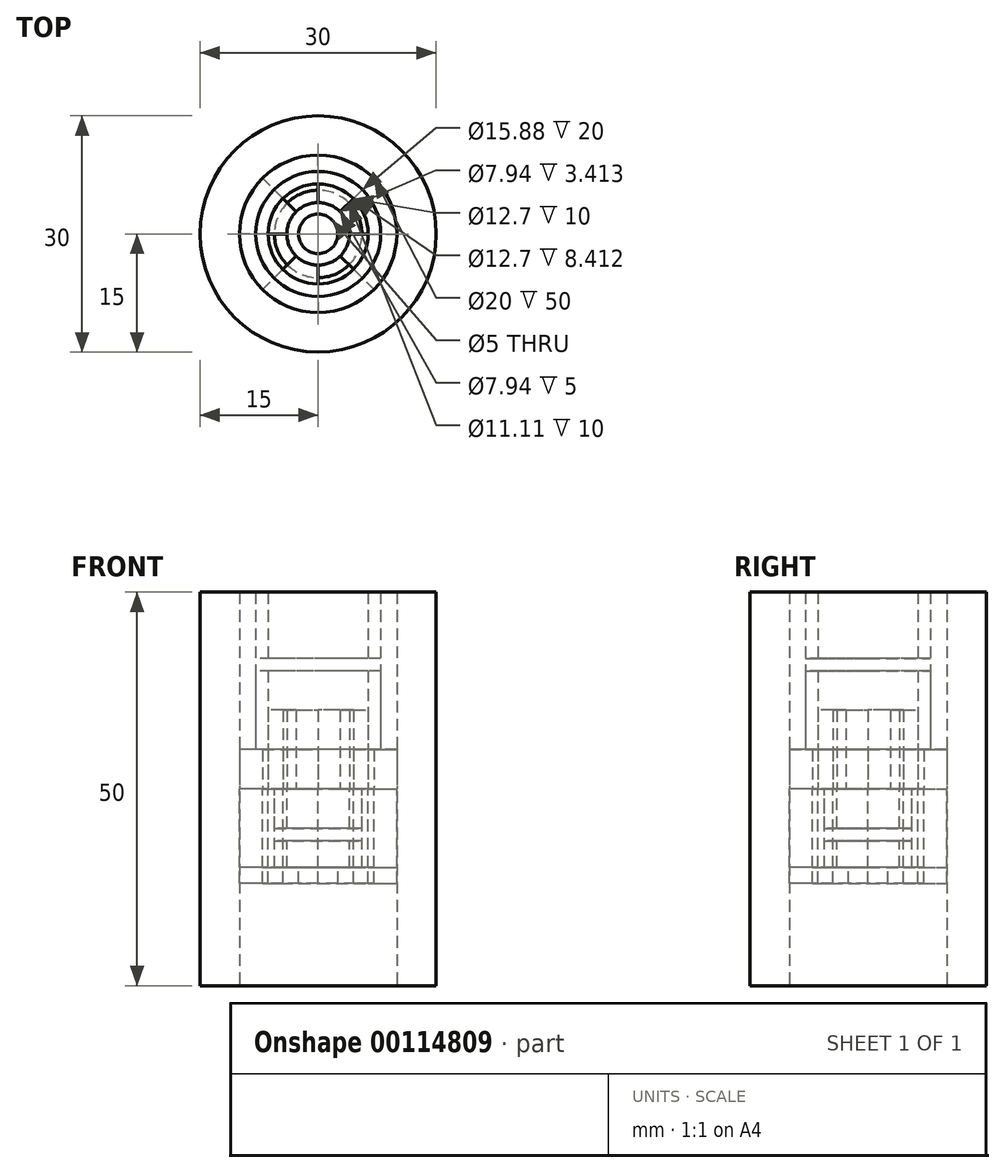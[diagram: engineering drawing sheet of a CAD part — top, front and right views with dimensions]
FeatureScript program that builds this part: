
annotation { "Feature Type Name" : "Feature", "Feature Type Description" : "" }
export const myFeature = defineFeature(function(context is Context, id is Id, definition is map)
    precondition{}
    {
        {
            var Q0;
            Q0=qCreatedBy(makeId("Top.planeOp"),FACE);
            var sketch = newSketch(context, id + "F0", { "sketchPlane" : qUnion([Q0])});
            skCircle(sketch, "E0", {"center": v(0, 0) * mm, "radius": 10 * mm});
            skCircle(sketch, "E1", {"center": v(0, 0) * mm, "radius": 3.97 * mm});
            skCircle(sketch, "E2", {"center": v(0, 0) * mm, "radius": 6.35 * mm});
            skCircle(sketch, "E3", {"center": v(0, 0) * mm, "radius": 7.94 * mm});
            skCircle(sketch, "E4", {"center": v(0, 0) * mm, "radius": 2.5 * mm});
            skLineSegment(sketch, "E5", {"start": v(0, 3.97) * mm, "end": v(0, 6.35) * mm});
            skLineSegment(sketch, "E6.1.0", {"start": v(-2.8, 2.8) * mm, "end": v(-4.5, 4.5) * mm});
            skLineSegment(sketch, "E6.2.0", {"start": v(-3.97, 0) * mm, "end": v(-6.35, 0) * mm});
            skLineSegment(sketch, "E6.3.0", {"start": v(-2.8, -2.8) * mm, "end": v(-4.5, -4.5) * mm});
            skLineSegment(sketch, "E6.4.0", {"start": v(0, -3.97) * mm, "end": v(0, -6.35) * mm});
            skLineSegment(sketch, "E6.5.0", {"start": v(2.8, -2.8) * mm, "end": v(4.5, -4.5) * mm});
            skLineSegment(sketch, "E6.6.0", {"start": v(3.97, 0) * mm, "end": v(6.35, 0) * mm});
            skLineSegment(sketch, "E6.7.0", {"start": v(2.8, 2.8) * mm, "end": v(4.5, 4.5) * mm});
            skCircle(sketch, "E7", {"center": v(0, 0) * mm, "radius": 15 * mm});
            skCircle(sketch, "E8", {"center": v(0, 0) * mm, "radius": 5.56 * mm});
            skLineSegment(sketch, "E9", {"start": v(0, 6.35) * mm, "end": v(0, 10) * mm});
            skLineSegment(sketch, "E10.1.0", {"start": v(-4.5, 4.5) * mm, "end": v(-7.07, 7.07) * mm});
            skLineSegment(sketch, "E10.2.0", {"start": v(-6.35, 0) * mm, "end": v(-10, 0) * mm});
            skLineSegment(sketch, "E11.1.3.0", {"start": v(-4.5, -4.5) * mm, "end": v(-7.07, -7.07) * mm});
            skLineSegment(sketch, "E11.1.4.0", {"start": v(0, -6.35) * mm, "end": v(0, -10) * mm});
            skLineSegment(sketch, "E11.1.5.0", {"start": v(4.5, -4.5) * mm, "end": v(7.07, -7.07) * mm});
            skLineSegment(sketch, "E11.1.6.0", {"start": v(6.35, 0) * mm, "end": v(10, 0) * mm});
            skLineSegment(sketch, "E11.1.7.0", {"start": v(4.5, 4.5) * mm, "end": v(7.07, 7.07) * mm});
            skSolve(sketch);
        }
        {
            var Q0;
            {var subQ0=sQuery(id+"F0.wireOp",EDGE,"E5");Q0=makeQuery(id+"F0.imprint","IMPRINT",FACE,{"disambiguationData":[TD([[makeQuery(id+"F0.imprint","IMPRINT",EDGE,{"derivedFrom":subQ0}),-1.0]])]});}
            var Q1;
            {var subQ0=sQuery(id+"F0.wireOp",EDGE,"E6.9.0");Q1=makeQuery(id+"F0.imprint","IMPRINT",FACE,{"disambiguationData":[TD([[makeQuery(id+"F0.imprint","IMPRINT",EDGE,{"derivedFrom":subQ0}),1.0]])]});}
            var Q2;
            {var subQ0=sQuery(id+"F0.wireOp",EDGE,"E6.7.0");Q2=makeQuery(id+"F0.imprint","IMPRINT",FACE,{"disambiguationData":[TD([[makeQuery(id+"F0.imprint","IMPRINT",EDGE,{"derivedFrom":subQ0}),1.0]])]});}
            var Q3;
            {var subQ0=sQuery(id+"F0.wireOp",EDGE,"E6.5.0");Q3=makeQuery(id+"F0.imprint","IMPRINT",FACE,{"disambiguationData":[TD([[makeQuery(id+"F0.imprint","IMPRINT",EDGE,{"derivedFrom":subQ0}),1.0]])]});}
            var Q4;
            {var subQ0=sQuery(id+"F0.wireOp",EDGE,"E6.3.0");Q4=makeQuery(id+"F0.imprint","IMPRINT",FACE,{"disambiguationData":[TD([[makeQuery(id+"F0.imprint","IMPRINT",EDGE,{"derivedFrom":subQ0}),1.0]])]});}
            var Q5;
            {var subQ0=sQuery(id+"F0.wireOp",EDGE,"E6.1.0");Q5=makeQuery(id+"F0.imprint","IMPRINT",FACE,{"disambiguationData":[TD([[makeQuery(id+"F0.imprint","IMPRINT",EDGE,{"derivedFrom":subQ0}),1.0]])]});}
            extrude(context, id + "F1", {"entities" : qUnion([Q0, Q1, Q2, Q3, Q4, Q5]), "depth" : 10 * mm});
        }
        {
            var Q0;
            Q0=makeQuery(id+"F0.imprint","IMPRINT",FACE,{"disambiguationData":[TD([[makeQuery(id+"F0.imprint","IMPRINT",EDGE,{"derivedFrom":sQuery(id+"F0.wireOp",EDGE,"E3")}),1.0]])]});
            extrude(context, id + "F2", {"entities" : qUnion([Q0]), "depth" : 15 * mm, "hasSecondDirection" : true, "secondDirectionOppositeDirection" : false, "secondDirectionDepth" : 5 * mm});
        }
        {
            var Q0;
            Q0=makeQuery(id+"F2.opExtrude","CAP_FACE",FACE,{"disambiguationData":[OSD([sQuery(id+"F0.wireOp",EDGE,"E2"),sQuery(id+"F0.wireOp",EDGE,"E3")])],"isStart":false});
            extrude(context, id + "F3", {"entities" : qUnion([Q0]), "operationType" : NewBodyOperationType.ADD, "depth" : 10 * mm, "hasSecondDirection" : true, "secondDirectionOppositeDirection" : false, "secondDirectionDepth" : 1.59 * mm});
        }
        {
            var Q0;
            Q0=makeQuery(id+"F0.imprint","IMPRINT",FACE,{"disambiguationData":[TD([[makeQuery(id+"F0.imprint","IMPRINT",EDGE,{"derivedFrom":sQuery(id+"F0.wireOp",EDGE,"E0")}),1.0]])]});
            extrude(context, id + "F4", {"entities" : qUnion([Q0]), "depth" : 25 * mm, "hasSecondDirection" : true, "secondDirectionOppositeDirection" : false, "secondDirectionDepth" : 5 * mm});
        }
        {
            var Q0;
            {var subQ0=sQuery(id+"F0.wireOp",EDGE,"E6.8.0");var subQ1=sQuery(id+"F0.wireOp",EDGE,"E1");var subQ2=makeQuery(id+"F0.imprint","INTERSECT",VERTEX,{"derivedFrom":[subQ1,subQ0]});Q0=makeQuery(id+"F0.imprint","IMPRINT",FACE,{"disambiguationData":[TD([[makeQuery(id+"F0.imprint","IMPRINT",EDGE,{"disambiguationData":[TD([[subQ2,-1.0]])],"derivedFrom":subQ1}),-1.0]])]});}
            var Q1;
            {var subQ0=sQuery(id+"F0.wireOp",EDGE,"E6.9.0");var subQ1=sQuery(id+"F0.wireOp",EDGE,"E1");var subQ2=makeQuery(id+"F0.imprint","INTERSECT",VERTEX,{"derivedFrom":[subQ1,subQ0]});Q1=makeQuery(id+"F0.imprint","IMPRINT",FACE,{"disambiguationData":[TD([[makeQuery(id+"F0.imprint","IMPRINT",EDGE,{"disambiguationData":[TD([[subQ2,-1.0]])],"derivedFrom":subQ1}),-1.0]])]});}
            var Q2;
            {var subQ0=sQuery(id+"F0.wireOp",EDGE,"E6.10.0");var subQ1=sQuery(id+"F0.wireOp",EDGE,"E1");var subQ2=makeQuery(id+"F0.imprint","INTERSECT",VERTEX,{"derivedFrom":[subQ1,subQ0]});Q2=makeQuery(id+"F0.imprint","IMPRINT",FACE,{"disambiguationData":[TD([[makeQuery(id+"F0.imprint","IMPRINT",EDGE,{"disambiguationData":[TD([[subQ2,-1.0]])],"derivedFrom":subQ1}),-1.0]])]});}
            var Q3;
            {var subQ0=sQuery(id+"F0.wireOp",EDGE,"E5");var subQ1=sQuery(id+"F0.wireOp",EDGE,"E1");var subQ2=makeQuery(id+"F0.imprint","INTERSECT",VERTEX,{"derivedFrom":[subQ1,subQ0]});Q3=makeQuery(id+"F0.imprint","IMPRINT",FACE,{"disambiguationData":[TD([[makeQuery(id+"F0.imprint","IMPRINT",EDGE,{"disambiguationData":[TD([[subQ2,1.0]])],"derivedFrom":subQ1}),-1.0]])]});}
            var Q4;
            {var subQ0=sQuery(id+"F0.wireOp",EDGE,"E5");var subQ1=sQuery(id+"F0.wireOp",EDGE,"E1");var subQ2=makeQuery(id+"F0.imprint","INTERSECT",VERTEX,{"derivedFrom":[subQ1,subQ0]});Q4=makeQuery(id+"F0.imprint","IMPRINT",FACE,{"disambiguationData":[TD([[makeQuery(id+"F0.imprint","IMPRINT",EDGE,{"disambiguationData":[TD([[subQ2,-1.0]])],"derivedFrom":subQ1}),-1.0]])]});}
            var Q5;
            {var subQ0=sQuery(id+"F0.wireOp",EDGE,"E6.1.0");var subQ1=sQuery(id+"F0.wireOp",EDGE,"E1");var subQ2=makeQuery(id+"F0.imprint","INTERSECT",VERTEX,{"derivedFrom":[subQ1,subQ0]});Q5=makeQuery(id+"F0.imprint","IMPRINT",FACE,{"disambiguationData":[TD([[makeQuery(id+"F0.imprint","IMPRINT",EDGE,{"disambiguationData":[TD([[subQ2,-1.0]])],"derivedFrom":subQ1}),-1.0]])]});}
            var Q6;
            {var subQ0=sQuery(id+"F0.wireOp",EDGE,"E6.2.0");var subQ1=sQuery(id+"F0.wireOp",EDGE,"E1");var subQ2=makeQuery(id+"F0.imprint","INTERSECT",VERTEX,{"derivedFrom":[subQ1,subQ0]});Q6=makeQuery(id+"F0.imprint","IMPRINT",FACE,{"disambiguationData":[TD([[makeQuery(id+"F0.imprint","IMPRINT",EDGE,{"disambiguationData":[TD([[subQ2,-1.0]])],"derivedFrom":subQ1}),-1.0]])]});}
            var Q7;
            {var subQ0=sQuery(id+"F0.wireOp",EDGE,"E6.3.0");var subQ1=sQuery(id+"F0.wireOp",EDGE,"E1");var subQ2=makeQuery(id+"F0.imprint","INTERSECT",VERTEX,{"derivedFrom":[subQ1,subQ0]});Q7=makeQuery(id+"F0.imprint","IMPRINT",FACE,{"disambiguationData":[TD([[makeQuery(id+"F0.imprint","IMPRINT",EDGE,{"disambiguationData":[TD([[subQ2,-1.0]])],"derivedFrom":subQ1}),-1.0]])]});}
            var Q8;
            {var subQ0=sQuery(id+"F0.wireOp",EDGE,"E6.4.0");var subQ1=sQuery(id+"F0.wireOp",EDGE,"E1");var subQ2=makeQuery(id+"F0.imprint","INTERSECT",VERTEX,{"derivedFrom":[subQ1,subQ0]});Q8=makeQuery(id+"F0.imprint","IMPRINT",FACE,{"disambiguationData":[TD([[makeQuery(id+"F0.imprint","IMPRINT",EDGE,{"disambiguationData":[TD([[subQ2,-1.0]])],"derivedFrom":subQ1}),-1.0]])]});}
            var Q9;
            {var subQ0=sQuery(id+"F0.wireOp",EDGE,"E6.5.0");var subQ1=sQuery(id+"F0.wireOp",EDGE,"E1");var subQ2=makeQuery(id+"F0.imprint","INTERSECT",VERTEX,{"derivedFrom":[subQ1,subQ0]});Q9=makeQuery(id+"F0.imprint","IMPRINT",FACE,{"disambiguationData":[TD([[makeQuery(id+"F0.imprint","IMPRINT",EDGE,{"disambiguationData":[TD([[subQ2,-1.0]])],"derivedFrom":subQ1}),-1.0]])]});}
            var Q10;
            {var subQ0=sQuery(id+"F0.wireOp",EDGE,"E6.6.0");var subQ1=sQuery(id+"F0.wireOp",EDGE,"E1");var subQ2=makeQuery(id+"F0.imprint","INTERSECT",VERTEX,{"derivedFrom":[subQ1,subQ0]});Q10=makeQuery(id+"F0.imprint","IMPRINT",FACE,{"disambiguationData":[TD([[makeQuery(id+"F0.imprint","IMPRINT",EDGE,{"disambiguationData":[TD([[subQ2,-1.0]])],"derivedFrom":subQ1}),-1.0]])]});}
            var Q11;
            {var subQ0=sQuery(id+"F0.wireOp",EDGE,"E6.7.0");var subQ1=sQuery(id+"F0.wireOp",EDGE,"E1");var subQ2=makeQuery(id+"F0.imprint","INTERSECT",VERTEX,{"derivedFrom":[subQ1,subQ0]});Q11=makeQuery(id+"F0.imprint","IMPRINT",FACE,{"disambiguationData":[TD([[makeQuery(id+"F0.imprint","IMPRINT",EDGE,{"disambiguationData":[TD([[subQ2,-1.0]])],"derivedFrom":subQ1}),-1.0]])]});}
            extrude(context, id + "F5", {"entities" : qUnion([Q0, Q1, Q2, Q3, Q4, Q5, Q6, Q7, Q8, Q9, Q10, Q11]), "oppositeDirection" : true, "depth" : 10 * mm, "hasSecondDirection" : true, "secondDirectionOppositeDirection" : true, "secondDirectionDepth" : 6.6 * mm});
        }
        {
            var Q0;
            {var subQ0=sQuery(id+"F0.wireOp",EDGE,"E6.8.0");var subQ1=sQuery(id+"F0.wireOp",EDGE,"E1");var subQ2=makeQuery(id+"F0.imprint","INTERSECT",VERTEX,{"derivedFrom":[subQ1,subQ0]});Q0=makeQuery(id+"F0.imprint","IMPRINT",FACE,{"disambiguationData":[TD([[makeQuery(id+"F0.imprint","IMPRINT",EDGE,{"disambiguationData":[TD([[subQ2,-1.0]])],"derivedFrom":subQ1}),-1.0]])]});}
            var Q1;
            {var subQ0=sQuery(id+"F0.wireOp",EDGE,"E6.9.0");var subQ1=sQuery(id+"F0.wireOp",EDGE,"E1");var subQ2=makeQuery(id+"F0.imprint","INTERSECT",VERTEX,{"derivedFrom":[subQ1,subQ0]});Q1=makeQuery(id+"F0.imprint","IMPRINT",FACE,{"disambiguationData":[TD([[makeQuery(id+"F0.imprint","IMPRINT",EDGE,{"disambiguationData":[TD([[subQ2,-1.0]])],"derivedFrom":subQ1}),-1.0]])]});}
            var Q2;
            {var subQ0=sQuery(id+"F0.wireOp",EDGE,"E6.10.0");var subQ1=sQuery(id+"F0.wireOp",EDGE,"E1");var subQ2=makeQuery(id+"F0.imprint","INTERSECT",VERTEX,{"derivedFrom":[subQ1,subQ0]});Q2=makeQuery(id+"F0.imprint","IMPRINT",FACE,{"disambiguationData":[TD([[makeQuery(id+"F0.imprint","IMPRINT",EDGE,{"disambiguationData":[TD([[subQ2,-1.0]])],"derivedFrom":subQ1}),-1.0]])]});}
            var Q3;
            {var subQ0=sQuery(id+"F0.wireOp",EDGE,"E5");var subQ1=sQuery(id+"F0.wireOp",EDGE,"E1");var subQ2=makeQuery(id+"F0.imprint","INTERSECT",VERTEX,{"derivedFrom":[subQ1,subQ0]});Q3=makeQuery(id+"F0.imprint","IMPRINT",FACE,{"disambiguationData":[TD([[makeQuery(id+"F0.imprint","IMPRINT",EDGE,{"disambiguationData":[TD([[subQ2,1.0]])],"derivedFrom":subQ1}),-1.0]])]});}
            var Q4;
            {var subQ0=sQuery(id+"F0.wireOp",EDGE,"E5");var subQ1=sQuery(id+"F0.wireOp",EDGE,"E1");var subQ2=makeQuery(id+"F0.imprint","INTERSECT",VERTEX,{"derivedFrom":[subQ1,subQ0]});Q4=makeQuery(id+"F0.imprint","IMPRINT",FACE,{"disambiguationData":[TD([[makeQuery(id+"F0.imprint","IMPRINT",EDGE,{"disambiguationData":[TD([[subQ2,-1.0]])],"derivedFrom":subQ1}),-1.0]])]});}
            var Q5;
            {var subQ0=sQuery(id+"F0.wireOp",EDGE,"E6.1.0");var subQ1=sQuery(id+"F0.wireOp",EDGE,"E1");var subQ2=makeQuery(id+"F0.imprint","INTERSECT",VERTEX,{"derivedFrom":[subQ1,subQ0]});Q5=makeQuery(id+"F0.imprint","IMPRINT",FACE,{"disambiguationData":[TD([[makeQuery(id+"F0.imprint","IMPRINT",EDGE,{"disambiguationData":[TD([[subQ2,-1.0]])],"derivedFrom":subQ1}),-1.0]])]});}
            var Q6;
            {var subQ0=sQuery(id+"F0.wireOp",EDGE,"E6.2.0");var subQ1=sQuery(id+"F0.wireOp",EDGE,"E1");var subQ2=makeQuery(id+"F0.imprint","INTERSECT",VERTEX,{"derivedFrom":[subQ1,subQ0]});Q6=makeQuery(id+"F0.imprint","IMPRINT",FACE,{"disambiguationData":[TD([[makeQuery(id+"F0.imprint","IMPRINT",EDGE,{"disambiguationData":[TD([[subQ2,-1.0]])],"derivedFrom":subQ1}),-1.0]])]});}
            var Q7;
            {var subQ0=sQuery(id+"F0.wireOp",EDGE,"E6.3.0");var subQ1=sQuery(id+"F0.wireOp",EDGE,"E1");var subQ2=makeQuery(id+"F0.imprint","INTERSECT",VERTEX,{"derivedFrom":[subQ1,subQ0]});Q7=makeQuery(id+"F0.imprint","IMPRINT",FACE,{"disambiguationData":[TD([[makeQuery(id+"F0.imprint","IMPRINT",EDGE,{"disambiguationData":[TD([[subQ2,-1.0]])],"derivedFrom":subQ1}),-1.0]])]});}
            var Q8;
            {var subQ0=sQuery(id+"F0.wireOp",EDGE,"E6.4.0");var subQ1=sQuery(id+"F0.wireOp",EDGE,"E1");var subQ2=makeQuery(id+"F0.imprint","INTERSECT",VERTEX,{"derivedFrom":[subQ1,subQ0]});Q8=makeQuery(id+"F0.imprint","IMPRINT",FACE,{"disambiguationData":[TD([[makeQuery(id+"F0.imprint","IMPRINT",EDGE,{"disambiguationData":[TD([[subQ2,-1.0]])],"derivedFrom":subQ1}),-1.0]])]});}
            var Q9;
            {var subQ0=sQuery(id+"F0.wireOp",EDGE,"E6.5.0");var subQ1=sQuery(id+"F0.wireOp",EDGE,"E1");var subQ2=makeQuery(id+"F0.imprint","INTERSECT",VERTEX,{"derivedFrom":[subQ1,subQ0]});Q9=makeQuery(id+"F0.imprint","IMPRINT",FACE,{"disambiguationData":[TD([[makeQuery(id+"F0.imprint","IMPRINT",EDGE,{"disambiguationData":[TD([[subQ2,-1.0]])],"derivedFrom":subQ1}),-1.0]])]});}
            var Q10;
            {var subQ0=sQuery(id+"F0.wireOp",EDGE,"E6.6.0");var subQ1=sQuery(id+"F0.wireOp",EDGE,"E1");var subQ2=makeQuery(id+"F0.imprint","INTERSECT",VERTEX,{"derivedFrom":[subQ1,subQ0]});Q10=makeQuery(id+"F0.imprint","IMPRINT",FACE,{"disambiguationData":[TD([[makeQuery(id+"F0.imprint","IMPRINT",EDGE,{"disambiguationData":[TD([[subQ2,-1.0]])],"derivedFrom":subQ1}),-1.0]])]});}
            var Q11;
            {var subQ0=sQuery(id+"F0.wireOp",EDGE,"E6.7.0");var subQ1=sQuery(id+"F0.wireOp",EDGE,"E1");var subQ2=makeQuery(id+"F0.imprint","INTERSECT",VERTEX,{"derivedFrom":[subQ1,subQ0]});Q11=makeQuery(id+"F0.imprint","IMPRINT",FACE,{"disambiguationData":[TD([[makeQuery(id+"F0.imprint","IMPRINT",EDGE,{"disambiguationData":[TD([[subQ2,-1.0]])],"derivedFrom":subQ1}),-1.0]])]});}
            extrude(context, id + "F6", {"entities" : qUnion([Q0, Q1, Q2, Q3, Q4, Q5, Q6, Q7, Q8, Q9, Q10, Q11]), "oppositeDirection" : true, "depth" : 5 * mm});
        }
        {
            var Q0;
            {var subQ0=sQuery(id+"F0.wireOp",EDGE,"E6.5.0");var subQ5=sQuery(id+"F0.wireOp",EDGE,"E8");var subQ6=makeQuery(id+"F0.imprint","INTERSECT",VERTEX,{"derivedFrom":[subQ0,subQ5]});Q0=makeQuery(id+"F0.imprint","IMPRINT",FACE,{"disambiguationData":[TD([[makeQuery(id+"F0.imprint","IMPRINT",EDGE,{"disambiguationData":[TD([[subQ6,-1.0]])],"derivedFrom":subQ5}),-1.0]])]});}
            var Q1;
            {var subQ0=sQuery(id+"F0.wireOp",EDGE,"E6.4.0");var subQ5=sQuery(id+"F0.wireOp",EDGE,"E8");var subQ6=makeQuery(id+"F0.imprint","INTERSECT",VERTEX,{"derivedFrom":[subQ0,subQ5]});Q1=makeQuery(id+"F0.imprint","IMPRINT",FACE,{"disambiguationData":[TD([[makeQuery(id+"F0.imprint","IMPRINT",EDGE,{"disambiguationData":[TD([[subQ6,-1.0]])],"derivedFrom":subQ5}),-1.0]])]});}
            var Q2;
            {var subQ0=sQuery(id+"F0.wireOp",EDGE,"E6.3.0");var subQ5=sQuery(id+"F0.wireOp",EDGE,"E8");var subQ6=makeQuery(id+"F0.imprint","INTERSECT",VERTEX,{"derivedFrom":[subQ0,subQ5]});Q2=makeQuery(id+"F0.imprint","IMPRINT",FACE,{"disambiguationData":[TD([[makeQuery(id+"F0.imprint","IMPRINT",EDGE,{"disambiguationData":[TD([[subQ6,-1.0]])],"derivedFrom":subQ5}),-1.0]])]});}
            var Q3;
            {var subQ0=sQuery(id+"F0.wireOp",EDGE,"E6.2.0");var subQ5=sQuery(id+"F0.wireOp",EDGE,"E8");var subQ6=makeQuery(id+"F0.imprint","INTERSECT",VERTEX,{"derivedFrom":[subQ0,subQ5]});Q3=makeQuery(id+"F0.imprint","IMPRINT",FACE,{"disambiguationData":[TD([[makeQuery(id+"F0.imprint","IMPRINT",EDGE,{"disambiguationData":[TD([[subQ6,-1.0]])],"derivedFrom":subQ5}),-1.0]])]});}
            var Q4;
            {var subQ0=sQuery(id+"F0.wireOp",EDGE,"E6.1.0");var subQ5=sQuery(id+"F0.wireOp",EDGE,"E8");var subQ6=makeQuery(id+"F0.imprint","INTERSECT",VERTEX,{"derivedFrom":[subQ0,subQ5]});Q4=makeQuery(id+"F0.imprint","IMPRINT",FACE,{"disambiguationData":[TD([[makeQuery(id+"F0.imprint","IMPRINT",EDGE,{"disambiguationData":[TD([[subQ6,-1.0]])],"derivedFrom":subQ5}),-1.0]])]});}
            var Q5;
            {var subQ0=sQuery(id+"F0.wireOp",EDGE,"E5");var subQ5=sQuery(id+"F0.wireOp",EDGE,"E8");var subQ6=makeQuery(id+"F0.imprint","INTERSECT",VERTEX,{"derivedFrom":[subQ0,subQ5]});Q5=makeQuery(id+"F0.imprint","IMPRINT",FACE,{"disambiguationData":[TD([[makeQuery(id+"F0.imprint","IMPRINT",EDGE,{"disambiguationData":[TD([[subQ6,-1.0]])],"derivedFrom":subQ5}),-1.0]])]});}
            var Q6;
            {var subQ0=sQuery(id+"F0.wireOp",EDGE,"E5");var subQ5=sQuery(id+"F0.wireOp",EDGE,"E8");var subQ7=makeQuery(id+"F0.imprint","INTERSECT",VERTEX,{"derivedFrom":[subQ0,subQ5]});Q6=makeQuery(id+"F0.imprint","IMPRINT",FACE,{"disambiguationData":[TD([[makeQuery(id+"F0.imprint","IMPRINT",EDGE,{"disambiguationData":[TD([[subQ7,1.0]])],"derivedFrom":subQ5}),-1.0]])]});}
            var Q7;
            {var subQ0=sQuery(id+"F0.wireOp",EDGE,"E6.6.0");var subQ5=sQuery(id+"F0.wireOp",EDGE,"E8");var subQ7=makeQuery(id+"F0.imprint","INTERSECT",VERTEX,{"derivedFrom":[subQ0,subQ5]});Q7=makeQuery(id+"F0.imprint","IMPRINT",FACE,{"disambiguationData":[TD([[makeQuery(id+"F0.imprint","IMPRINT",EDGE,{"disambiguationData":[TD([[subQ7,-1.0]])],"derivedFrom":subQ5}),-1.0]])]});}
            var Q8;
            {var subQ0=sQuery(id+"F0.wireOp",EDGE,"E9");var subQ1=sQuery(id+"F0.wireOp",EDGE,"E0");var subQ2=makeQuery(id+"F0.imprint","INTERSECT",VERTEX,{"derivedFrom":[subQ1,subQ0]});Q8=makeQuery(id+"F0.imprint","IMPRINT",FACE,{"disambiguationData":[TD([[makeQuery(id+"F0.imprint","IMPRINT",EDGE,{"disambiguationData":[TD([[subQ2,1.0]])],"derivedFrom":subQ1}),1.0]])]});}
            var Q9;
            {var subQ3=sQuery(id+"F0.wireOp",EDGE,"E11.1.7.0");var subQ5=sQuery(id+"F0.wireOp",EDGE,"E3");var subQ6=makeQuery(id+"F0.imprint","INTERSECT",VERTEX,{"derivedFrom":[subQ5,subQ3]});Q9=makeQuery(id+"F0.imprint","IMPRINT",FACE,{"disambiguationData":[TD([[makeQuery(id+"F0.imprint","IMPRINT",EDGE,{"disambiguationData":[TD([[subQ6,-1.0]])],"derivedFrom":subQ5}),1.0]])]});}
            var Q10;
            {var subQ0=sQuery(id+"F0.wireOp",EDGE,"E10.1.0");var subQ5=sQuery(id+"F0.wireOp",EDGE,"E3");var subQ6=makeQuery(id+"F0.imprint","INTERSECT",VERTEX,{"derivedFrom":[subQ5,subQ0]});Q10=makeQuery(id+"F0.imprint","IMPRINT",FACE,{"disambiguationData":[TD([[makeQuery(id+"F0.imprint","IMPRINT",EDGE,{"disambiguationData":[TD([[subQ6,-1.0]])],"derivedFrom":subQ5}),1.0]])]});}
            var Q11;
            {var subQ0=sQuery(id+"F0.wireOp",EDGE,"E10.1.0");var subQ1=sQuery(id+"F0.wireOp",EDGE,"E0");var subQ2=makeQuery(id+"F0.imprint","INTERSECT",VERTEX,{"derivedFrom":[subQ1,subQ0]});Q11=makeQuery(id+"F0.imprint","IMPRINT",FACE,{"disambiguationData":[TD([[makeQuery(id+"F0.imprint","IMPRINT",EDGE,{"disambiguationData":[TD([[subQ2,-1.0]])],"derivedFrom":subQ1}),1.0]])]});}
            var Q12;
            {var subQ0=sQuery(id+"F0.wireOp",EDGE,"E11.1.3.0");var subQ1=sQuery(id+"F0.wireOp",EDGE,"E0");var subQ2=makeQuery(id+"F0.imprint","INTERSECT",VERTEX,{"derivedFrom":[subQ1,subQ0]});Q12=makeQuery(id+"F0.imprint","IMPRINT",FACE,{"disambiguationData":[TD([[makeQuery(id+"F0.imprint","IMPRINT",EDGE,{"disambiguationData":[TD([[subQ2,-1.0]])],"derivedFrom":subQ1}),1.0]])]});}
            var Q13;
            {var subQ0=sQuery(id+"F0.wireOp",EDGE,"E11.1.3.0");var subQ5=sQuery(id+"F0.wireOp",EDGE,"E3");var subQ6=makeQuery(id+"F0.imprint","INTERSECT",VERTEX,{"derivedFrom":[subQ5,subQ0]});Q13=makeQuery(id+"F0.imprint","IMPRINT",FACE,{"disambiguationData":[TD([[makeQuery(id+"F0.imprint","IMPRINT",EDGE,{"disambiguationData":[TD([[subQ6,-1.0]])],"derivedFrom":subQ5}),1.0]])]});}
            var Q14;
            {var subQ0=sQuery(id+"F0.wireOp",EDGE,"E11.1.5.0");var subQ1=sQuery(id+"F0.wireOp",EDGE,"E0");var subQ2=makeQuery(id+"F0.imprint","INTERSECT",VERTEX,{"derivedFrom":[subQ1,subQ0]});Q14=makeQuery(id+"F0.imprint","IMPRINT",FACE,{"disambiguationData":[TD([[makeQuery(id+"F0.imprint","IMPRINT",EDGE,{"disambiguationData":[TD([[subQ2,-1.0]])],"derivedFrom":subQ1}),1.0]])]});}
            var Q15;
            {var subQ3=sQuery(id+"F0.wireOp",EDGE,"E11.1.6.0");var subQ5=sQuery(id+"F0.wireOp",EDGE,"E3");var subQ7=makeQuery(id+"F0.imprint","INTERSECT",VERTEX,{"derivedFrom":[subQ5,subQ3]});Q15=makeQuery(id+"F0.imprint","IMPRINT",FACE,{"disambiguationData":[TD([[makeQuery(id+"F0.imprint","IMPRINT",EDGE,{"disambiguationData":[TD([[subQ7,1.0]])],"derivedFrom":subQ5}),1.0]])]});}
            extrude(context, id + "F7", {"entities" : qUnion([Q0, Q1, Q2, Q3, Q4, Q5, Q6, Q7, Q8, Q9, Q10, Q11, Q12, Q13, Q14, Q15]), "oppositeDirection" : true, "depth" : 10 * mm});
        }
        {
            var Q0;
            {var subQ0=sQuery(id+"F0.wireOp",EDGE,"E9");var subQ1=sQuery(id+"F0.wireOp",EDGE,"E0");var subQ2=makeQuery(id+"F0.imprint","INTERSECT",VERTEX,{"derivedFrom":[subQ1,subQ0]});Q0=makeQuery(id+"F0.imprint","IMPRINT",FACE,{"disambiguationData":[TD([[makeQuery(id+"F0.imprint","IMPRINT",EDGE,{"disambiguationData":[TD([[subQ2,1.0]])],"derivedFrom":subQ1}),1.0]])]});}
            var Q1;
            {var subQ3=sQuery(id+"F0.wireOp",EDGE,"E11.1.7.0");var subQ5=sQuery(id+"F0.wireOp",EDGE,"E3");var subQ6=makeQuery(id+"F0.imprint","INTERSECT",VERTEX,{"derivedFrom":[subQ5,subQ3]});Q1=makeQuery(id+"F0.imprint","IMPRINT",FACE,{"disambiguationData":[TD([[makeQuery(id+"F0.imprint","IMPRINT",EDGE,{"disambiguationData":[TD([[subQ6,-1.0]])],"derivedFrom":subQ5}),1.0]])]});}
            var Q2;
            {var subQ0=sQuery(id+"F0.wireOp",EDGE,"E11.1.5.0");var subQ1=sQuery(id+"F0.wireOp",EDGE,"E0");var subQ2=makeQuery(id+"F0.imprint","INTERSECT",VERTEX,{"derivedFrom":[subQ1,subQ0]});Q2=makeQuery(id+"F0.imprint","IMPRINT",FACE,{"disambiguationData":[TD([[makeQuery(id+"F0.imprint","IMPRINT",EDGE,{"disambiguationData":[TD([[subQ2,-1.0]])],"derivedFrom":subQ1}),1.0]])]});}
            var Q3;
            {var subQ3=sQuery(id+"F0.wireOp",EDGE,"E11.1.6.0");var subQ5=sQuery(id+"F0.wireOp",EDGE,"E3");var subQ7=makeQuery(id+"F0.imprint","INTERSECT",VERTEX,{"derivedFrom":[subQ5,subQ3]});Q3=makeQuery(id+"F0.imprint","IMPRINT",FACE,{"disambiguationData":[TD([[makeQuery(id+"F0.imprint","IMPRINT",EDGE,{"disambiguationData":[TD([[subQ7,1.0]])],"derivedFrom":subQ5}),1.0]])]});}
            var Q4;
            {var subQ0=sQuery(id+"F0.wireOp",EDGE,"E11.1.3.0");var subQ1=sQuery(id+"F0.wireOp",EDGE,"E0");var subQ2=makeQuery(id+"F0.imprint","INTERSECT",VERTEX,{"derivedFrom":[subQ1,subQ0]});Q4=makeQuery(id+"F0.imprint","IMPRINT",FACE,{"disambiguationData":[TD([[makeQuery(id+"F0.imprint","IMPRINT",EDGE,{"disambiguationData":[TD([[subQ2,-1.0]])],"derivedFrom":subQ1}),1.0]])]});}
            var Q5;
            {var subQ0=sQuery(id+"F0.wireOp",EDGE,"E11.1.3.0");var subQ5=sQuery(id+"F0.wireOp",EDGE,"E3");var subQ6=makeQuery(id+"F0.imprint","INTERSECT",VERTEX,{"derivedFrom":[subQ5,subQ0]});Q5=makeQuery(id+"F0.imprint","IMPRINT",FACE,{"disambiguationData":[TD([[makeQuery(id+"F0.imprint","IMPRINT",EDGE,{"disambiguationData":[TD([[subQ6,-1.0]])],"derivedFrom":subQ5}),1.0]])]});}
            var Q6;
            {var subQ0=sQuery(id+"F0.wireOp",EDGE,"E10.1.0");var subQ1=sQuery(id+"F0.wireOp",EDGE,"E0");var subQ2=makeQuery(id+"F0.imprint","INTERSECT",VERTEX,{"derivedFrom":[subQ1,subQ0]});Q6=makeQuery(id+"F0.imprint","IMPRINT",FACE,{"disambiguationData":[TD([[makeQuery(id+"F0.imprint","IMPRINT",EDGE,{"disambiguationData":[TD([[subQ2,-1.0]])],"derivedFrom":subQ1}),1.0]])]});}
            var Q7;
            {var subQ0=sQuery(id+"F0.wireOp",EDGE,"E10.1.0");var subQ5=sQuery(id+"F0.wireOp",EDGE,"E3");var subQ6=makeQuery(id+"F0.imprint","INTERSECT",VERTEX,{"derivedFrom":[subQ5,subQ0]});Q7=makeQuery(id+"F0.imprint","IMPRINT",FACE,{"disambiguationData":[TD([[makeQuery(id+"F0.imprint","IMPRINT",EDGE,{"disambiguationData":[TD([[subQ6,-1.0]])],"derivedFrom":subQ5}),1.0]])]});}
            extrude(context, id + "F8", {"entities" : qUnion([Q0, Q1, Q2, Q3, Q4, Q5, Q6, Q7]), "depth" : 5 * mm});
        }
        {
            var Q0;
            {var subQ0=sQuery(id+"F0.wireOp",EDGE,"E5");var subQ5=sQuery(id+"F0.wireOp",EDGE,"E8");var subQ7=makeQuery(id+"F0.imprint","INTERSECT",VERTEX,{"derivedFrom":[subQ0,subQ5]});Q0=makeQuery(id+"F0.imprint","IMPRINT",FACE,{"disambiguationData":[TD([[makeQuery(id+"F0.imprint","IMPRINT",EDGE,{"disambiguationData":[TD([[subQ7,1.0]])],"derivedFrom":subQ5}),-1.0]])]});}
            var Q1;
            {var subQ0=sQuery(id+"F0.wireOp",EDGE,"E5");var subQ5=sQuery(id+"F0.wireOp",EDGE,"E8");var subQ6=makeQuery(id+"F0.imprint","INTERSECT",VERTEX,{"derivedFrom":[subQ0,subQ5]});Q1=makeQuery(id+"F0.imprint","IMPRINT",FACE,{"disambiguationData":[TD([[makeQuery(id+"F0.imprint","IMPRINT",EDGE,{"disambiguationData":[TD([[subQ6,-1.0]])],"derivedFrom":subQ5}),-1.0]])]});}
            var Q2;
            {var subQ0=sQuery(id+"F0.wireOp",EDGE,"E6.1.0");var subQ5=sQuery(id+"F0.wireOp",EDGE,"E8");var subQ6=makeQuery(id+"F0.imprint","INTERSECT",VERTEX,{"derivedFrom":[subQ0,subQ5]});Q2=makeQuery(id+"F0.imprint","IMPRINT",FACE,{"disambiguationData":[TD([[makeQuery(id+"F0.imprint","IMPRINT",EDGE,{"disambiguationData":[TD([[subQ6,-1.0]])],"derivedFrom":subQ5}),-1.0]])]});}
            var Q3;
            {var subQ0=sQuery(id+"F0.wireOp",EDGE,"E6.2.0");var subQ5=sQuery(id+"F0.wireOp",EDGE,"E8");var subQ6=makeQuery(id+"F0.imprint","INTERSECT",VERTEX,{"derivedFrom":[subQ0,subQ5]});Q3=makeQuery(id+"F0.imprint","IMPRINT",FACE,{"disambiguationData":[TD([[makeQuery(id+"F0.imprint","IMPRINT",EDGE,{"disambiguationData":[TD([[subQ6,-1.0]])],"derivedFrom":subQ5}),-1.0]])]});}
            var Q4;
            {var subQ0=sQuery(id+"F0.wireOp",EDGE,"E6.3.0");var subQ5=sQuery(id+"F0.wireOp",EDGE,"E8");var subQ6=makeQuery(id+"F0.imprint","INTERSECT",VERTEX,{"derivedFrom":[subQ0,subQ5]});Q4=makeQuery(id+"F0.imprint","IMPRINT",FACE,{"disambiguationData":[TD([[makeQuery(id+"F0.imprint","IMPRINT",EDGE,{"disambiguationData":[TD([[subQ6,-1.0]])],"derivedFrom":subQ5}),-1.0]])]});}
            var Q5;
            {var subQ0=sQuery(id+"F0.wireOp",EDGE,"E6.4.0");var subQ5=sQuery(id+"F0.wireOp",EDGE,"E8");var subQ6=makeQuery(id+"F0.imprint","INTERSECT",VERTEX,{"derivedFrom":[subQ0,subQ5]});Q5=makeQuery(id+"F0.imprint","IMPRINT",FACE,{"disambiguationData":[TD([[makeQuery(id+"F0.imprint","IMPRINT",EDGE,{"disambiguationData":[TD([[subQ6,-1.0]])],"derivedFrom":subQ5}),-1.0]])]});}
            var Q6;
            {var subQ0=sQuery(id+"F0.wireOp",EDGE,"E6.5.0");var subQ5=sQuery(id+"F0.wireOp",EDGE,"E8");var subQ6=makeQuery(id+"F0.imprint","INTERSECT",VERTEX,{"derivedFrom":[subQ0,subQ5]});Q6=makeQuery(id+"F0.imprint","IMPRINT",FACE,{"disambiguationData":[TD([[makeQuery(id+"F0.imprint","IMPRINT",EDGE,{"disambiguationData":[TD([[subQ6,-1.0]])],"derivedFrom":subQ5}),-1.0]])]});}
            var Q7;
            {var subQ0=sQuery(id+"F0.wireOp",EDGE,"E6.6.0");var subQ5=sQuery(id+"F0.wireOp",EDGE,"E8");var subQ7=makeQuery(id+"F0.imprint","INTERSECT",VERTEX,{"derivedFrom":[subQ0,subQ5]});Q7=makeQuery(id+"F0.imprint","IMPRINT",FACE,{"disambiguationData":[TD([[makeQuery(id+"F0.imprint","IMPRINT",EDGE,{"disambiguationData":[TD([[subQ7,-1.0]])],"derivedFrom":subQ5}),-1.0]])]});}
            var Q8;
            {var subQ0=sQuery(id+"F0.wireOp",EDGE,"E6.6.0");var subQ1=sQuery(id+"F0.wireOp",EDGE,"E1");var subQ2=makeQuery(id+"F0.imprint","INTERSECT",VERTEX,{"derivedFrom":[subQ1,subQ0]});Q8=makeQuery(id+"F0.imprint","IMPRINT",FACE,{"disambiguationData":[TD([[makeQuery(id+"F0.imprint","IMPRINT",EDGE,{"disambiguationData":[TD([[subQ2,-1.0]])],"derivedFrom":subQ1}),-1.0]])]});}
            var Q9;
            {var subQ0=sQuery(id+"F0.wireOp",EDGE,"E5");var subQ1=sQuery(id+"F0.wireOp",EDGE,"E1");var subQ2=makeQuery(id+"F0.imprint","INTERSECT",VERTEX,{"derivedFrom":[subQ1,subQ0]});Q9=makeQuery(id+"F0.imprint","IMPRINT",FACE,{"disambiguationData":[TD([[makeQuery(id+"F0.imprint","IMPRINT",EDGE,{"disambiguationData":[TD([[subQ2,1.0]])],"derivedFrom":subQ1}),-1.0]])]});}
            var Q10;
            {var subQ0=sQuery(id+"F0.wireOp",EDGE,"E5");var subQ1=sQuery(id+"F0.wireOp",EDGE,"E1");var subQ2=makeQuery(id+"F0.imprint","INTERSECT",VERTEX,{"derivedFrom":[subQ1,subQ0]});Q10=makeQuery(id+"F0.imprint","IMPRINT",FACE,{"disambiguationData":[TD([[makeQuery(id+"F0.imprint","IMPRINT",EDGE,{"disambiguationData":[TD([[subQ2,-1.0]])],"derivedFrom":subQ1}),-1.0]])]});}
            var Q11;
            {var subQ0=sQuery(id+"F0.wireOp",EDGE,"E6.1.0");var subQ1=sQuery(id+"F0.wireOp",EDGE,"E1");var subQ2=makeQuery(id+"F0.imprint","INTERSECT",VERTEX,{"derivedFrom":[subQ1,subQ0]});Q11=makeQuery(id+"F0.imprint","IMPRINT",FACE,{"disambiguationData":[TD([[makeQuery(id+"F0.imprint","IMPRINT",EDGE,{"disambiguationData":[TD([[subQ2,-1.0]])],"derivedFrom":subQ1}),-1.0]])]});}
            var Q12;
            {var subQ0=sQuery(id+"F0.wireOp",EDGE,"E6.2.0");var subQ1=sQuery(id+"F0.wireOp",EDGE,"E1");var subQ2=makeQuery(id+"F0.imprint","INTERSECT",VERTEX,{"derivedFrom":[subQ1,subQ0]});Q12=makeQuery(id+"F0.imprint","IMPRINT",FACE,{"disambiguationData":[TD([[makeQuery(id+"F0.imprint","IMPRINT",EDGE,{"disambiguationData":[TD([[subQ2,-1.0]])],"derivedFrom":subQ1}),-1.0]])]});}
            var Q13;
            {var subQ0=sQuery(id+"F0.wireOp",EDGE,"E6.3.0");var subQ1=sQuery(id+"F0.wireOp",EDGE,"E1");var subQ2=makeQuery(id+"F0.imprint","INTERSECT",VERTEX,{"derivedFrom":[subQ1,subQ0]});Q13=makeQuery(id+"F0.imprint","IMPRINT",FACE,{"disambiguationData":[TD([[makeQuery(id+"F0.imprint","IMPRINT",EDGE,{"disambiguationData":[TD([[subQ2,-1.0]])],"derivedFrom":subQ1}),-1.0]])]});}
            var Q14;
            {var subQ0=sQuery(id+"F0.wireOp",EDGE,"E6.4.0");var subQ1=sQuery(id+"F0.wireOp",EDGE,"E1");var subQ2=makeQuery(id+"F0.imprint","INTERSECT",VERTEX,{"derivedFrom":[subQ1,subQ0]});Q14=makeQuery(id+"F0.imprint","IMPRINT",FACE,{"disambiguationData":[TD([[makeQuery(id+"F0.imprint","IMPRINT",EDGE,{"disambiguationData":[TD([[subQ2,-1.0]])],"derivedFrom":subQ1}),-1.0]])]});}
            var Q15;
            {var subQ0=sQuery(id+"F0.wireOp",EDGE,"E6.5.0");var subQ1=sQuery(id+"F0.wireOp",EDGE,"E1");var subQ2=makeQuery(id+"F0.imprint","INTERSECT",VERTEX,{"derivedFrom":[subQ1,subQ0]});Q15=makeQuery(id+"F0.imprint","IMPRINT",FACE,{"disambiguationData":[TD([[makeQuery(id+"F0.imprint","IMPRINT",EDGE,{"disambiguationData":[TD([[subQ2,-1.0]])],"derivedFrom":subQ1}),-1.0]])]});}
            var Q16;
            Q16=makeQuery(id+"F0.imprint","IMPRINT",FACE,{"disambiguationData":[TD([[makeQuery(id+"F0.imprint","IMPRINT",EDGE,{"derivedFrom":sQuery(id+"F0.wireOp",EDGE,"E4")}),-1.0]])]});
            var Q17;
            {var subQ0=sQuery(id+"F0.wireOp",EDGE,"E9");var subQ1=sQuery(id+"F0.wireOp",EDGE,"E0");var subQ2=makeQuery(id+"F0.imprint","INTERSECT",VERTEX,{"derivedFrom":[subQ1,subQ0]});Q17=makeQuery(id+"F0.imprint","IMPRINT",FACE,{"disambiguationData":[TD([[makeQuery(id+"F0.imprint","IMPRINT",EDGE,{"disambiguationData":[TD([[subQ2,1.0]])],"derivedFrom":subQ1}),1.0]])]});}
            var Q18;
            {var subQ3=sQuery(id+"F0.wireOp",EDGE,"E11.1.7.0");var subQ5=sQuery(id+"F0.wireOp",EDGE,"E3");var subQ6=makeQuery(id+"F0.imprint","INTERSECT",VERTEX,{"derivedFrom":[subQ5,subQ3]});Q18=makeQuery(id+"F0.imprint","IMPRINT",FACE,{"disambiguationData":[TD([[makeQuery(id+"F0.imprint","IMPRINT",EDGE,{"disambiguationData":[TD([[subQ6,-1.0]])],"derivedFrom":subQ5}),1.0]])]});}
            var Q19;
            {var subQ3=sQuery(id+"F0.wireOp",EDGE,"E11.1.6.0");var subQ5=sQuery(id+"F0.wireOp",EDGE,"E3");var subQ7=makeQuery(id+"F0.imprint","INTERSECT",VERTEX,{"derivedFrom":[subQ5,subQ3]});Q19=makeQuery(id+"F0.imprint","IMPRINT",FACE,{"disambiguationData":[TD([[makeQuery(id+"F0.imprint","IMPRINT",EDGE,{"disambiguationData":[TD([[subQ7,1.0]])],"derivedFrom":subQ5}),1.0]])]});}
            var Q20;
            {var subQ0=sQuery(id+"F0.wireOp",EDGE,"E11.1.5.0");var subQ1=sQuery(id+"F0.wireOp",EDGE,"E0");var subQ2=makeQuery(id+"F0.imprint","INTERSECT",VERTEX,{"derivedFrom":[subQ1,subQ0]});Q20=makeQuery(id+"F0.imprint","IMPRINT",FACE,{"disambiguationData":[TD([[makeQuery(id+"F0.imprint","IMPRINT",EDGE,{"disambiguationData":[TD([[subQ2,-1.0]])],"derivedFrom":subQ1}),1.0]])]});}
            var Q21;
            {var subQ0=sQuery(id+"F0.wireOp",EDGE,"E11.1.3.0");var subQ5=sQuery(id+"F0.wireOp",EDGE,"E3");var subQ6=makeQuery(id+"F0.imprint","INTERSECT",VERTEX,{"derivedFrom":[subQ5,subQ0]});Q21=makeQuery(id+"F0.imprint","IMPRINT",FACE,{"disambiguationData":[TD([[makeQuery(id+"F0.imprint","IMPRINT",EDGE,{"disambiguationData":[TD([[subQ6,-1.0]])],"derivedFrom":subQ5}),1.0]])]});}
            var Q22;
            {var subQ0=sQuery(id+"F0.wireOp",EDGE,"E10.1.0");var subQ1=sQuery(id+"F0.wireOp",EDGE,"E0");var subQ2=makeQuery(id+"F0.imprint","INTERSECT",VERTEX,{"derivedFrom":[subQ1,subQ0]});Q22=makeQuery(id+"F0.imprint","IMPRINT",FACE,{"disambiguationData":[TD([[makeQuery(id+"F0.imprint","IMPRINT",EDGE,{"disambiguationData":[TD([[subQ2,-1.0]])],"derivedFrom":subQ1}),1.0]])]});}
            var Q23;
            {var subQ0=sQuery(id+"F0.wireOp",EDGE,"E10.1.0");var subQ5=sQuery(id+"F0.wireOp",EDGE,"E3");var subQ6=makeQuery(id+"F0.imprint","INTERSECT",VERTEX,{"derivedFrom":[subQ5,subQ0]});Q23=makeQuery(id+"F0.imprint","IMPRINT",FACE,{"disambiguationData":[TD([[makeQuery(id+"F0.imprint","IMPRINT",EDGE,{"disambiguationData":[TD([[subQ6,-1.0]])],"derivedFrom":subQ5}),1.0]])]});}
            var Q24;
            {var subQ0=sQuery(id+"F0.wireOp",EDGE,"E11.1.3.0");var subQ1=sQuery(id+"F0.wireOp",EDGE,"E0");var subQ2=makeQuery(id+"F0.imprint","INTERSECT",VERTEX,{"derivedFrom":[subQ1,subQ0]});Q24=makeQuery(id+"F0.imprint","IMPRINT",FACE,{"disambiguationData":[TD([[makeQuery(id+"F0.imprint","IMPRINT",EDGE,{"disambiguationData":[TD([[subQ2,-1.0]])],"derivedFrom":subQ1}),1.0]])]});}
            extrude(context, id + "F9", {"entities" : qUnion([Q0, Q1, Q2, Q3, Q4, Q5, Q6, Q7, Q8, Q9, Q10, Q11, Q12, Q13, Q14, Q15, Q16, Q17, Q18, Q19, Q20, Q21, Q22, Q23, Q24]), "oppositeDirection" : true, "depth" : 12 * mm, "hasSecondDirection" : true, "secondDirectionOppositeDirection" : true, "secondDirectionDepth" : 10 * mm});
        }
        {
            var Q0;
            Q0=makeQuery(id+"F0.imprint","IMPRINT",FACE,{"disambiguationData":[TD([[makeQuery(id+"F0.imprint","IMPRINT",EDGE,{"derivedFrom":sQuery(id+"F0.wireOp",EDGE,"E7")}),1.0]])]});
            extrude(context, id + "F10", {"entities" : qUnion([Q0]), "depth" : 25 * mm, "hasSecondDirection" : true, "secondDirectionOppositeDirection" : true, "secondDirectionDepth" : 25 * mm});
        }
    });
